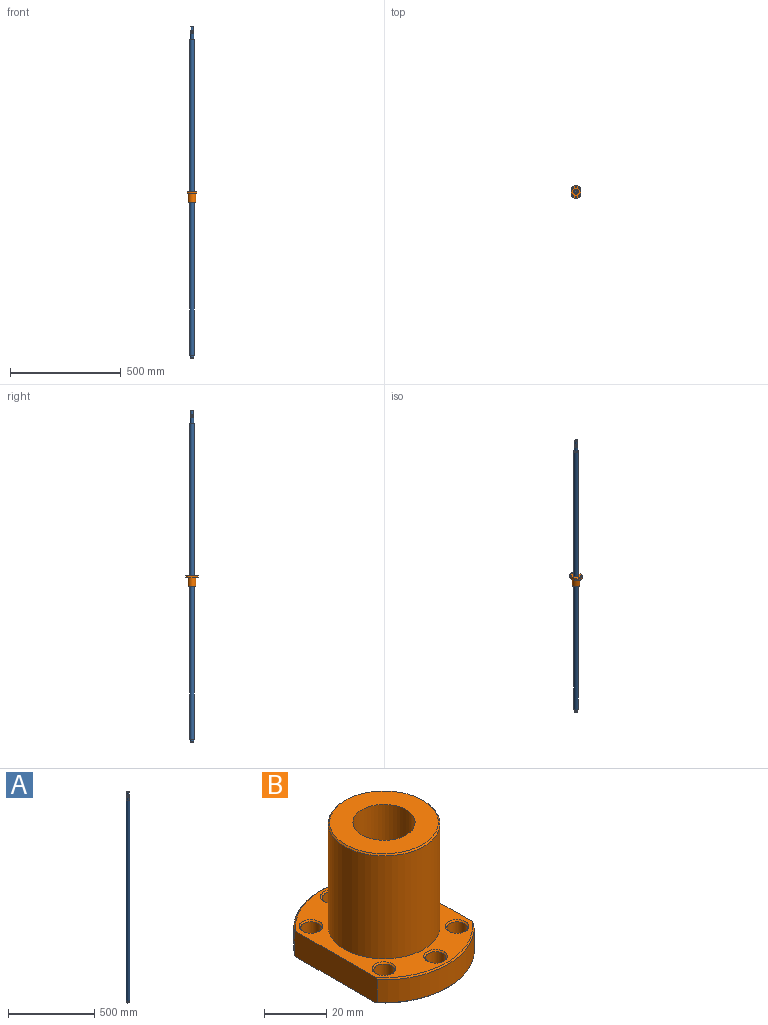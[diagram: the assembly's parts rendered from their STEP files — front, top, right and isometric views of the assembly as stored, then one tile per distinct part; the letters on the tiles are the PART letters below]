
ASSEMBLY  parts=2 mates=1
PART A: 32 faces, bbox 20x20x1500 mm
  f0: cone r=5.5mm half-angle=45deg, axis (0,0,-1), area 25.5mm2, adj f5,f25
  f1: cone r=7mm half-angle=45deg, axis (0,0,1), area 32.2mm2, adj f2,f27
  f2: cylinder r=7.5mm len=15mm, axis (0,0,1), area 110.7mm2, adj f1,f28
  f3: cylinder r=7.15mm len=14.3mm, axis (0,0,1), area 51.7mm2, adj f26,f28
  f4: cylinder r=7.5mm len=15mm, axis (0,0,1), area 424.1mm2, adj f23,f26
  f5: cylinder r=6mm len=19.5mm, axis (0,0,-1), area 735.1mm2, adj f0,f24
  f6: cylinder r=10mm len=1427mm, axis (0,0,-1), area 89661.1mm2, adj f22,f23
  f7: cylinder r=7.5mm len=26.26mm, axis (0,0,-1), area 1213.9mm2, adj f8,f22,f29,f30
  f8: cylinder r=7.5mm len=15mm, axis (0,0,-1), area 0.9mm2, adj f7,f9,f30,f31
  f9: cylinder r=7.5mm len=15mm, axis (0,0,-1), area 0.9mm2, adj f8,f10,f30,f31
  f10: cylinder r=7.5mm len=15mm, axis (0,0,-1), area 0.9mm2, adj f9,f11,f30,f31
  f11: cylinder r=7.5mm len=15mm, axis (0,0,-1), area 0.9mm2, adj f10,f12,f30,f31
  f12: cylinder r=7.5mm len=15mm, axis (0,0,-1), area 0.9mm2, adj f11,f13,f30,f31
  f13: cylinder r=7.5mm len=15mm, axis (0,0,-1), area 0.9mm2, adj f12,f14,f30,f31
  f14: cylinder r=7.5mm len=15mm, axis (0,0,-1), area 0.9mm2, adj f13,f15,f30,f31
  f15: cylinder r=7.5mm len=15mm, axis (0,0,-1), area 0.9mm2, adj f14,f16,f30,f31
  f16: cylinder r=7.5mm len=15mm, axis (0,0,-1), area 0.9mm2, adj f15,f17,f30,f31
  f17: cylinder r=7.5mm len=15mm, axis (0,0,-1), area 0.9mm2, adj f16,f18,f30,f31
  f18: cylinder r=7.5mm len=15mm, axis (0,0,-1), area 0.9mm2, adj f17,f19,f30,f31
  f19: cylinder r=7.5mm len=15mm, axis (0,0,-1), area 0.9mm2, adj f18,f20,f30,f31
  f20: cylinder r=7.5mm len=15mm, axis (0,0,-1), area 0.9mm2, adj f19,f21,f30,f31
  f21: cylinder r=7.5mm len=15mm, axis (0,0,-1), area 0.7mm2, adj f20,f24,f30,f31
  f22: plane 20x20mm, normal (0,0,1), area 137.4mm2, adj f6,f7
  f23: plane 20x20mm, normal (0,0,-1), area 137.4mm2, adj f4,f6
  f24: plane 14.06x14.03mm, normal (0,0,1), area 41.6mm2, adj f5,f21,f30,f31
  f25: plane 11x11mm, normal (0,0,1), area 95mm2, adj f0
  f26: plane 15x15mm, normal (0,0,-1), area 16.1mm2, adj f3,f4
  f27: plane 14x14mm, normal (0,0,-1), area 153.9mm2, adj f1
  f28: plane 15x15mm, normal (0,0,1), area 16.1mm2, adj f2,f3
  f29: plane 1x0.98mm, normal (0,1,0), area 0.5mm2, adj f7,f30,f31
  f30: bspline ~15.23x15mm, area 707.7mm2, adj f7,f8,f9,f10,f11,f12,f13,f14
  f31: bspline ~15x15mm, area 684.5mm2, adj f8,f9,f10,f11,f12,f13,f14,f15
PART B: 32 faces, bbox 44.8x58x51 mm
  f0: cone r=3.3mm half-angle=45deg, axis (0,0,-1), area 15.8mm2, adj f14,f22
  f1: cone r=3.3mm half-angle=45deg, axis (0,0,-1), area 15.8mm2, adj f17,f22
  f2: cone r=3.3mm half-angle=45deg, axis (0,0,-1), area 15.8mm2, adj f16,f22
  f3: cone r=3.3mm half-angle=45deg, axis (0,0,-1), area 15.8mm2, adj f15,f22
  f4: cone r=17.5mm half-angle=45deg, axis (0,0,-1), area 78.9mm2, adj f19,f27
  f5: cone r=3.3mm half-angle=45deg, axis (0,0,1), area 15.8mm2, adj f18,f21
  f6: cone r=3.3mm half-angle=45deg, axis (0,0,1), area 15.8mm2, adj f15,f21
  f7: cone r=3.3mm half-angle=45deg, axis (0,0,1), area 15.8mm2, adj f16,f21
  f8: cone r=3.3mm half-angle=45deg, axis (0,0,1), area 15.8mm2, adj f17,f21
  f9: cone r=3.3mm half-angle=45deg, axis (0,0,1), area 15.8mm2, adj f14,f21
  f10: cone r=3.3mm half-angle=45deg, axis (0,0,1), area 15.8mm2, adj f13,f21
  f11: cone r=3.3mm half-angle=45deg, axis (0,0,-1), area 15.8mm2, adj f13,f22
  f12: cone r=3.3mm half-angle=45deg, axis (0,0,-1), area 15.8mm2, adj f18,f22
  f13: cylinder r=3.3mm len=9mm, axis (0,0,-1), area 186.6mm2, adj f10,f11
  f14: cylinder r=3.3mm len=9mm, axis (0,0,-1), area 186.6mm2, adj f0,f9
  f15: cylinder r=3.3mm len=9mm, axis (0,0,-1), area 186.6mm2, adj f3,f6
  f16: cylinder r=3.3mm len=9mm, axis (0,0,-1), area 186.6mm2, adj f2,f7
  f17: cylinder r=3.3mm len=9mm, axis (0,0,-1), area 186.6mm2, adj f1,f8
  f18: cylinder r=3.3mm len=9mm, axis (0,0,-1), area 186.6mm2, adj f5,f12
  f19: cylinder r=18mm len=40.5mm, axis (0,0,-1), area 4580.4mm2, adj f4,f21
  f20: cylinder r=10mm len=51mm, axis (0,0,-1), area 3204.4mm2, adj f22,f27
  f21: plane 57x44mm, normal (0,0,1), area 939.7mm2, adj f5,f6,f7,f8,f9,f10,f19,f24
  f22: plane 57x44mm, normal (0,0,-1), area 1643.4mm2, adj f0,f1,f2,f3,f11,f12,f20,f24
  f23: cylinder r=29mm len=44mm, axis (0,0,-1), area 449.5mm2, adj f24,f26,f29,f30
  f24: plane 37.8x10.01mm, normal (-1,0,0), area 377.1mm2, adj f21,f22,f23,f25,f28,f29,f30,f31
  f25: cylinder r=29mm len=44mm, axis (0,0,-1), area 449.5mm2, adj f24,f26,f28,f31
  f26: plane 37.8x10.01mm, normal (1,0,0), area 377.1mm2, adj f21,f22,f23,f25,f28,f29,f30,f31
  f27: plane 35x35mm, normal (0,0,1), area 648mm2, adj f4,f20
  f28: cone r=28.5mm half-angle=45deg, axis (0,0,-1), area 35.4mm2, adj f21,f24,f25,f26
  f29: cone r=28.5mm half-angle=45deg, axis (0,0,-1), area 35.4mm2, adj f21,f23,f24,f26
  f30: cone r=29mm half-angle=45deg, axis (0,0,1), area 35.4mm2, adj f22,f23,f24,f26
  f31: cone r=29mm half-angle=45deg, axis (0,0,1), area 35.4mm2, adj f22,f24,f25,f26
PLACE A t=(23.63,161.15,439.37)mm
PLACE B rot(axis=(0,-1,0),180deg) t=(23.63,161.15,1178.37)mm
MATE cylindrical A.f0 <-> B.f4  axis (0,0,-1) through (23.63,161.15,1152.87)mm
